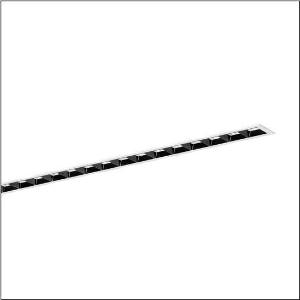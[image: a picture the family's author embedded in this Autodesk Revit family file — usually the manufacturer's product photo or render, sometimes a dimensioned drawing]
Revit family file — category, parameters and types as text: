
# Revit family: silica_r__21_51mx11tbt5w_4029
name_source: partatom
category: Lighting Fixtures
units: mm (PartAtom-declared; Revit-internal decimal feet)

## family parameters
Cut with Voids When Loaded = No
Host = Face
Light Source = No
Part Type = Normal
Room Calculation Point = No
Round Connector Dimension = Use Diameter
Shared = No

## types (1)
- --- (1 x LED, 4650 lm, 40.3 W, 6500K)
    Apparent Load = 40 VA
    CIE Flux Codes = 85 99 100 100 100
    Color Rendering = 80
    Color Temperature = 6500K
    Default Elevation = 1800 mm
    Description = Silica® 21, office luminaire, primary light control with darklight reflector, of PMMA, black, CAT 2 (L<= 3000cd/m²), light emission: direct distribution, primary light characteristic: symmetric, installation type: recessed, LED, rated luminous flux: 4.650lm, luminous efficacy: 110lm/W, light colour: 8tw, colour temperature: 2700..6500K, with terminal, 3+2-pole, max. 2.5mm², mains connection: 220..240V, AC, 50/60Hz, rated input power: 42.3W, luminaire housing, of aluminium, traffic white (RAL 9016), length: 1.528mm, width: 79mm, height: 53mm, protection rating (complete): IP20, insulation class (complete): insulation class I (protective earthing), certification: CE, permissible operating ambient temperature: 0..+35°C, standard: EN 50419, packaging unit: 1 piece
    Height = 0 mm  [stored 0 ft]
    Lamp = 1 x LED
    Lamp Light Flux = 4650 lm
    Lamp Power = 40.3 W
    Lamp count = 1
    Length = 1527 mm
    Luminous efficacy = 115 lm/W
    Manufacturer = Siteco
    ModVariant = No
    Model = 51MX11TBT5W
    Mounting Place = Ceiling
    Mounting Type = Recessed
    Number of Poles = 1
    OnlyDefault = Yes
    Power Factor = 1
    Product Name = Silica® 21
    Product group = office luminaire | ceiling recessed
    ProductGroupID = 401
    Protection Class = Protection class I
    Protection Degree = IP 20
    RLX_Detail_Level = 1
    RLX_Emergency_Light_Flux = 0 lm
    RLX_Emergency_Type = 0
    RLX_Emergency_Type_DB = No
    RlxData = <blob elided: 39021 chars, md5=14609460>
    Socket = socket
    Standby Power = 0 W
    System Light Flux = 4650 lm
    System Power = 40 W
    Type Comments = individual setting
    Type Image = l_1297791.jpg
    URL = http://relux.com
    VarID = @adj_071425
    Voltage = 0 V
    Weight = 0.00 kg
    Width = 79 mm

note: [stored X ft] marks values corroborated as IEEE doubles in the binary element streams (Revit-internal decimal feet)

## geometry (parser evidence)
native form markers: Blend x4, Sweep x11
no freeform markers — native parametric forms only
